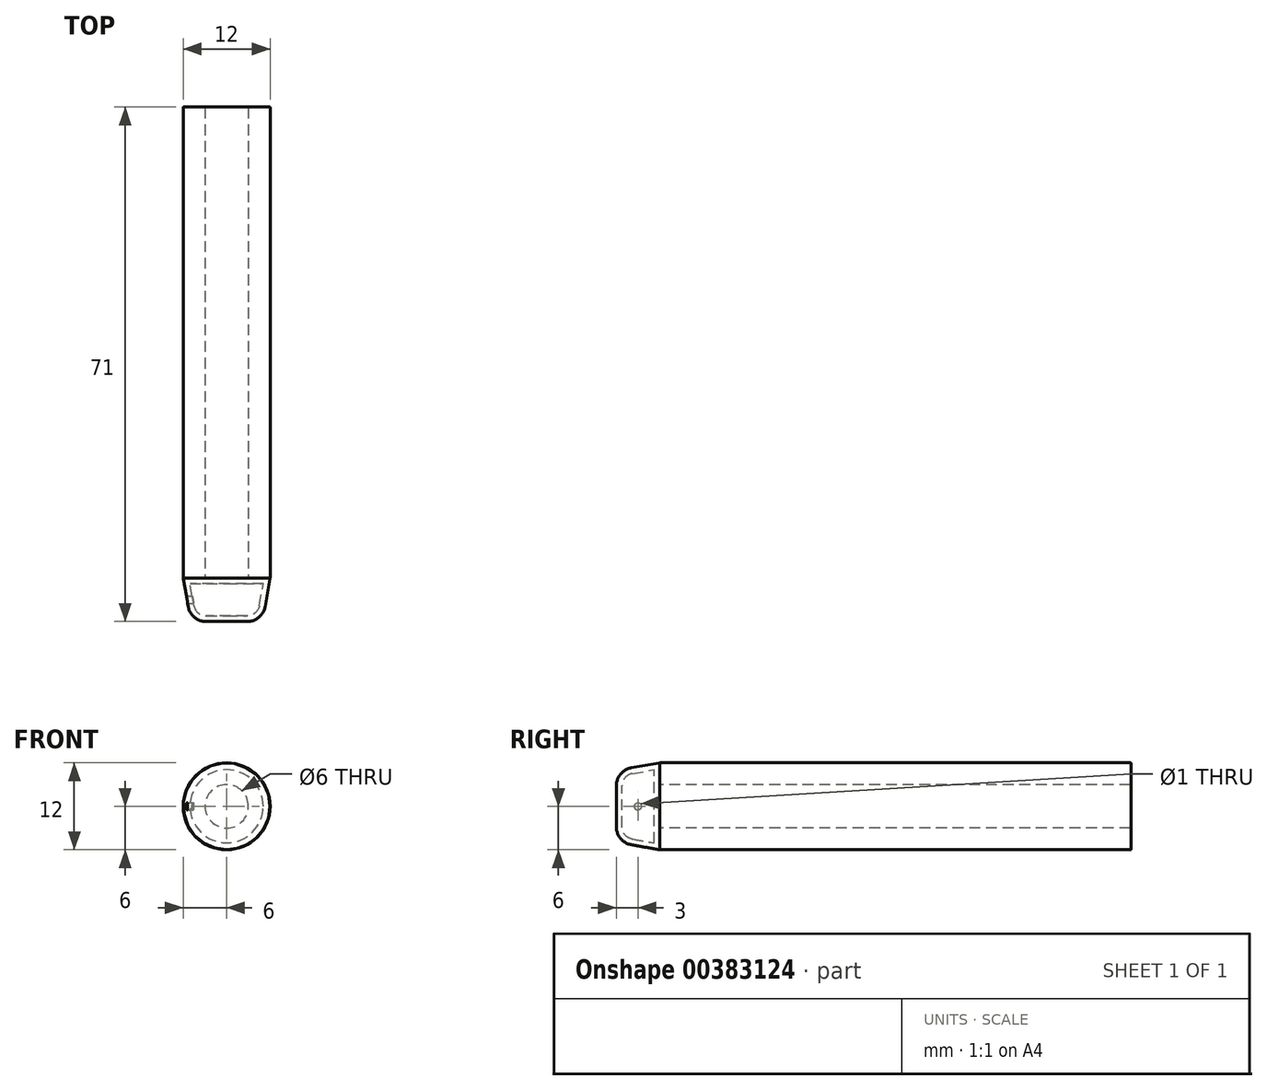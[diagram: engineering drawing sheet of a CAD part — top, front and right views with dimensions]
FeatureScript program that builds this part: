
annotation { "Feature Type Name" : "Feature", "Feature Type Description" : "" }
export const myFeature = defineFeature(function(context is Context, id is Id, definition is map)
    precondition{}
    {
        {
            var Q0;
            Q0=qCreatedBy(makeId("Front.planeOp"),FACE);
            var sketch = newSketch(context, id + "F0", { "sketchPlane" : qUnion([Q0])});
            skCircle(sketch, "E0", {"center": v(0, 0) * mm, "radius": 3 * mm});
            skCircle(sketch, "E1", {"center": v(0, 0) * mm, "radius": 6 * mm});
            skSolve(sketch);
        }
        {
            var Q0;
            Q0=qSketchRegion(id+"F0",true);
            extrude(context, id + "F1", {"entities" : qUnion([Q0]), "oppositeDirection" : true, "depth" : 65 * mm});
        }
        {
            var Q0;
            Q0=qSketchRegion(id+"F0",true);
            var Q1;
            Q1=makeQuery(id+"F0.imprint","IMPRINT",FACE,{"disambiguationData":[TD([[makeQuery(id+"F0.imprint","IMPRINT",EDGE,{"derivedFrom":sQuery(id+"F0.wireOp",EDGE,"E0")}),1.0]])]});
            extrude(context, id + "F2", {"entities" : qUnion([Q0, Q1]), "depth" : 6 * mm, "hasDraft" : true, "draftAngle" : 10 * degree, "draftPullDirection" : true});
        }
        {
            var Q0;
            Q0=makeQuery(id+"F2.opExtrude","CAP_EDGE",EDGE,{"disambiguationData":[OSD([sQuery(id+"F0.wireOp",EDGE,"E1")])],"isStart":false});
            fillet(context, id + "F3", {"entities" : qUnion([Q0]), "radius" : 2.5 * mm, "tangentPropagation" : true, "allowEdgeOverflow" : false});
        }
        {
            var Q0;
            Q0=makeQuery(id+"F2.opExtrude","CAP_FACE",FACE,{"disambiguationData":[OSD([sQuery(id+"F0.wireOp",EDGE,"E1")])],"isStart":true});
            var Q1;
            Q1=makeQuery(id+"F2.opExtrude","SWEPT_BODY",BODY,{"disambiguationData":[OSD([sQuery(id+"F0.wireOp",EDGE,"E1")])]});
            shell(context, id + "F4", {"isHollow" : true, "entities" : qUnion([Q0]), "parts" : qUnion([Q1]), "thickness" : 0.8 * mm});
        }
        {
            var Q0;
            Q0=qCreatedBy(makeId("Right.planeOp"),FACE);
            var sketch = newSketch(context, id + "F5", { "sketchPlane" : qUnion([Q0])});
            skCircle(sketch, "E2", {"center": v(-3, 0) * mm, "radius": 0.5 * mm});
            skSolve(sketch);
        }
        {
            var Q0;
            Q0=qSketchRegion(id+"F5",true);
            var Q1;
            Q1=makeQuery(id+"F2.opExtrude","SWEPT_FACE",FACE,{"disambiguationData":[OSD([sQuery(id+"F0.wireOp",EDGE,"E1")])]});
            extrude(context, id + "F6", {"entities" : qUnion([Q0]), "operationType" : NewBodyOperationType.REMOVE, "endBound" : BoundingType.UP_TO_SURFACE, "oppositeDirection" : true, "endBoundEntityFace" : qUnion([Q1]), "depth" : 25 * mm});
        }
        {
            var Q0;
            Q0=makeQuery(id+"F1.opExtrude","SWEPT_FACE",FACE,{"disambiguationData":[OSD([sQuery(id+"F0.wireOp",EDGE,"E1")])]});
            var Q1;
            Q1=makeQuery(id+"F1.opExtrude","SWEPT_FACE",FACE,{"disambiguationData":[OSD([sQuery(id+"F0.wireOp",EDGE,"E0")])]});
            var Q2;
            Q2=makeQuery(id+"F2.opExtrude","CAP_FACE",FACE,{"disambiguationData":[OSD([sQuery(id+"F0.wireOp",EDGE,"E1")])],"isStart":true});
            fillet(context, id + "F7", {"entities" : qUnion([Q0, Q1, Q2]), "radius" : 0.1 * mm, "tangentPropagation" : true, "allowEdgeOverflow" : false});
        }
    });
